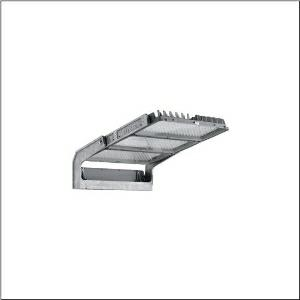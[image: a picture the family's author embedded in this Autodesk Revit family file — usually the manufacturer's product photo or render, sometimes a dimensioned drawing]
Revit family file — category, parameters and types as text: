
# Revit family: floodlight_fl_11_maxi_pro___rs08_5xa779224l01ab_f570
name_source: partatom
category: Lighting Fixtures
units: mm (PartAtom-declared; Revit-internal decimal feet)

## family parameters
Cut with Voids When Loaded = No
Host = Face
Light Source = No
Part Type = Normal
Room Calculation Point = No
Round Connector Dimension = Use Diameter
Shared = No

## types (1)
- --- (1 x LED, 152180 lm, 1633.1 W, 5700K)
    Apparent Load = 1633 VA
    CIE Flux Codes = 70 87 98 100 100
    Color Rendering = 90
    Color Temperature = 5700K
    Default Elevation = 1800 mm
    Description = Floodlight FL 11  maxi  pro floodlight; light control with lens of PMMA; cover panel of toughened safety glass, transparent; light distribution: RS08, rotationally symmetric direct distribution, LEDcolour temperature: 5700K, rated luminous flux: 152.180lm, colour rendering: CRI > 90, light colour: 957; luminous efficacy: 93lm/W; brightness control: DMX+RDM; with terminal, 8-pole, max. 2.5mm², mains connection: 220..240V/380..400V AC, 50/60Hz, surge voltage resistance: line to ground: 10kV, service life up to 100,000h L90. Typical operating time: 1000h per year, ECG replaceable separately, LED unit replaceable without ESD environment, dustproof LED module, dimming range 10..100%; 1633W floodlight with 3x LED unit of diecast aluminium, coated grey; length: 1.003mm / width: 651mm / height: 338mm; mounting bracket, of diecast aluminium, uncoated, natural, protection rating (complete): IP66; insulation class (complete): insulation class I (protective earthing); certification: CE, ENEC, VDE; ball protection: ball impact resistant, only for outdoor installations in the designated locations, permissible operating ambient temperature: -40..+55°C, permissible storage temperature: -40..+85°Cpackaging unit: 1 piece

Light Distribution: RS08
    Height = 320 mm
    Lamp = 1 x LED
    Lamp Light Flux = 152180 lm
    Lamp Power = 1633.1 W
    Lamp count = 1
    Length = 1002 mm
    Luminous efficacy = 93 lm/W
    Manufacturer = Siteco
    ModVariant = No
    Model = 5XA779224L01AB
    Mounting Place = Ceiling
    Mounting Type = Surface mounted
    Number of Poles = 1
    OnlyDefault = Yes
    Power Factor = 1
    Product Name = Floodlight FL 11 maxi pro | RS08
    Product group = floodlight | ceiling mounted
    ProductGroupID = 301
    Protection Class = Protection class I
    Protection Degree = IP 66
    RLX_Detail_Level = 1
    RLX_Emergency_Light_Flux = 0 lm
    RLX_Emergency_Type = 0
    RLX_Emergency_Type_DB = No
    RlxData = <blob elided: 40301 chars, md5=f1322d72>
    Socket = socket
    Standby Power = 0 W
    System Light Flux = 152180 lm
    System Power = 1633 W
    Type Comments = factory setting: luminous flux: 100 % | dim-lin: 255 | 1100 mA
    Type Image = l_1356210.jpg
    URL = http://relux.com
    VarID = @adj_014343
    Voltage = 0 V
    Weight = 0.00 kg
    Width = 655 mm

## geometry (parser evidence)
native form markers: Blend x4, Sweep x14
no freeform markers — native parametric forms only
